# Revit family: Wing C200EC_wall
name_source: partatom
category: Mechanical Equipment
revit_build: Autodesk Revit 2017 (Build: 20160720_1515(x64)
units: mm (PartAtom-declared; Revit-internal decimal feet)

## family parameters
Cut with Voids When Loaded = No
Host = Face
OmniClass Number = 23.75.70.21.17
OmniClass Title = Air Curtains
Part Type = Normal
Room Calculation Point = No
Round Connector Dimension = Use Diameter
Shared = No

## types (3) — shared parameters
Default Elevation = 1 m
Electrical Potential = 230 V
Frequency = 50 Hz
Manufacturer = VTS
Model = WING C200EC
Motor rated current EC = 2 A
Protection rating EC = 20
URL = http://vtsgroup.com
W = 2 m
Weight = 47.00 kg
zero-valued in all types: a

## per-type parameters (varying)
| type | FAN speed | Horizontal range | Vertical range |
| WING C200EC HIGH | HIGH | 4 m | 4 m |
| WING C200EC MEDIUM | MEDIUM | 3 m | 3 m |
| WING C200EC LOW | LOW | 2 m | 2 m |

## geometry (parser evidence)
native form markers: Sweep x7
no freeform markers — native parametric forms only
